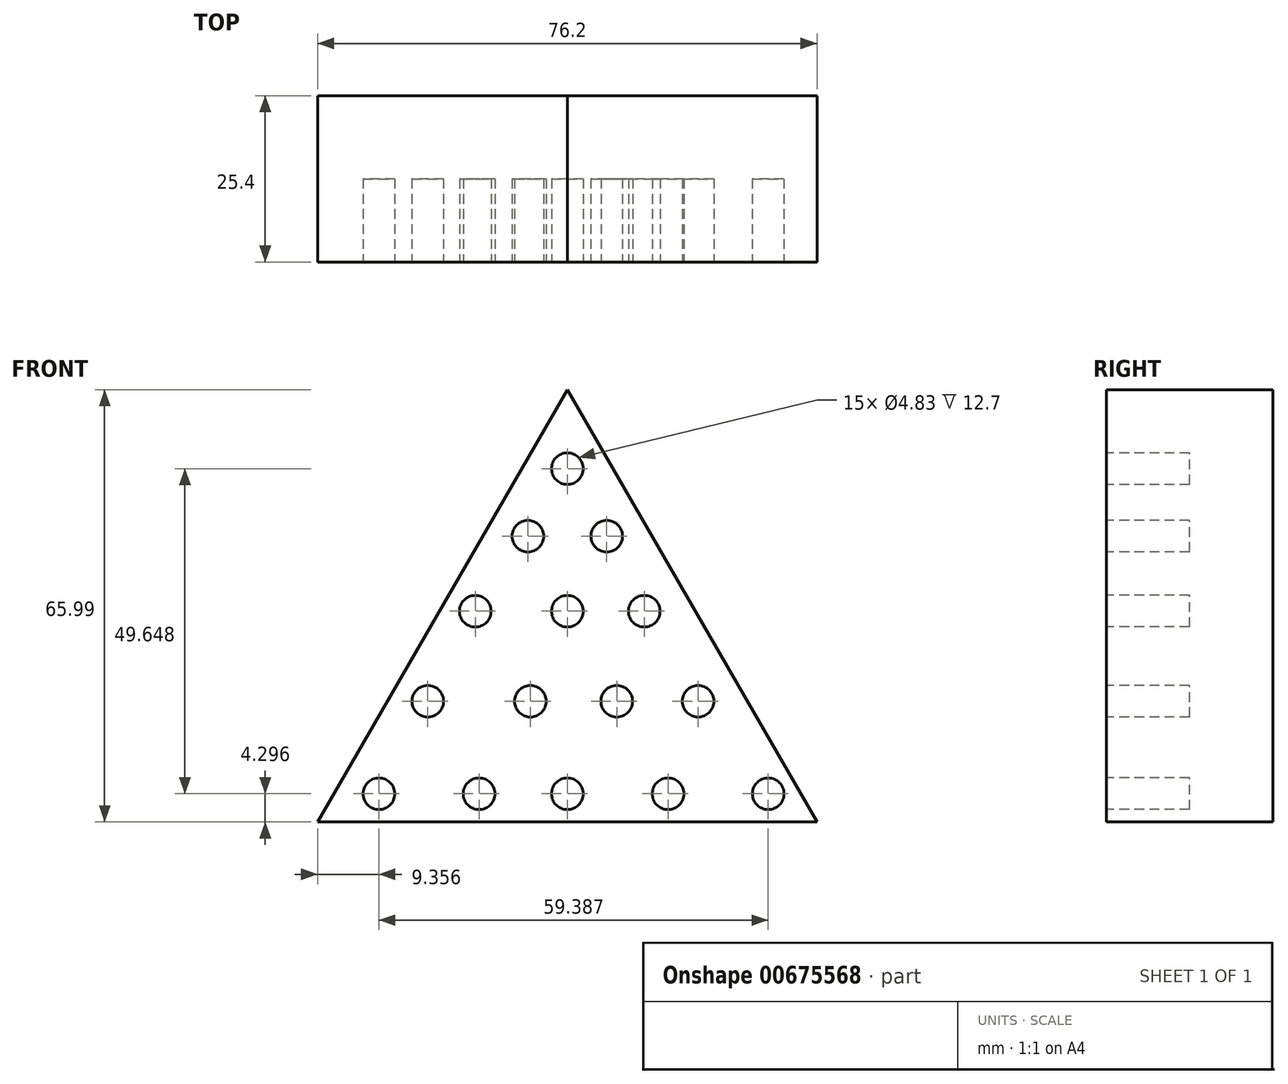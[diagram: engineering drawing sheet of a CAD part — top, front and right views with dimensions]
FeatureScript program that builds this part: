
annotation { "Feature Type Name" : "Feature", "Feature Type Description" : "" }
export const myFeature = defineFeature(function(context is Context, id is Id, definition is map)
    precondition{}
    {
        {
            var Q0;
            Q0=qCreatedBy(makeId("Front.planeOp"),FACE);
            var sketch = newSketch(context, id + "F0", { "sketchPlane" : qUnion([Q0])});
            skLineSegment(sketch, "E0", {"start": v(-73.23, 0) * mm, "end": v(2.97, 0) * mm});
            skLineSegment(sketch, "E1", {"start": v(2.97, 0) * mm, "end": v(-35.13, 66) * mm});
            skLineSegment(sketch, "E2", {"start": v(-35.13, 66) * mm, "end": v(-73.23, 0) * mm});
            skSolve(sketch);
        }
        {
            var Q0;
            Q0 = qSketchRegion(id + "F0", true);
            extrude(context, id + "F1", {"entities" : qUnion([Q0]), "depth" : 25.4 * mm, "offsetDistance" : 25.4 * mm});
        }
        {
            var Q0;
            Q0=makeQuery(id+"F1.opExtrude","CAP_FACE",FACE,{"disambiguationData":[OSD([sQuery(id+"F0.wireOp",EDGE,"E0"),sQuery(id+"F0.wireOp",EDGE,"E1"),sQuery(id+"F0.wireOp",EDGE,"E2")])],"isStart":false});
            var sketch = newSketch(context, id + "F2", { "sketchPlane" : qUnion([Q0])});
            skCircle(sketch, "E3", {"center": v(-63.87, 4.3) * mm, "radius": 2.41 * mm});
            skCircle(sketch, "E4", {"center": v(-48.6, 4.3) * mm, "radius": 2.41 * mm});
            skCircle(sketch, "E5", {"center": v(-35.13, 4.3) * mm, "radius": 2.41 * mm});
            skCircle(sketch, "E6", {"center": v(-19.76, 4.3) * mm, "radius": 2.41 * mm});
            skCircle(sketch, "E7", {"center": v(-4.49, 4.3) * mm, "radius": 2.41 * mm});
            skSolve(sketch);
        }
        {
            var Q0;
            Q0 = qSketchRegion(id + "F2", true);
            extrude(context, id + "F3", {"entities" : qUnion([Q0]), "operationType" : NewBodyOperationType.REMOVE, "oppositeDirection" : true, "depth" : 12.7 * mm, "offsetDistance" : 25.4 * mm});
        }
        {
            var Q0;
            Q0=makeQuery(id+"F1.opExtrude","CAP_FACE",FACE,{"disambiguationData":[OSD([sQuery(id+"F0.wireOp",EDGE,"E0"),sQuery(id+"F0.wireOp",EDGE,"E1"),sQuery(id+"F0.wireOp",EDGE,"E2")])],"isStart":false});
            var sketch = newSketch(context, id + "F4", { "sketchPlane" : qUnion([Q0])});
            skCircle(sketch, "E8", {"center": v(-56.43, 18.43) * mm, "radius": 2.41 * mm});
            skCircle(sketch, "E9", {"center": v(-40.77, 18.43) * mm, "radius": 2.41 * mm});
            skCircle(sketch, "E10", {"center": v(-27.6, 18.43) * mm, "radius": 2.41 * mm});
            skCircle(sketch, "E11", {"center": v(-15.18, 18.43) * mm, "radius": 2.41 * mm});
            skCircle(sketch, "E12", {"center": v(-23.4, 32.18) * mm, "radius": 2.41 * mm});
            skCircle(sketch, "E13", {"center": v(-35.13, 32.18) * mm, "radius": 2.41 * mm});
            skCircle(sketch, "E14", {"center": v(-49.17, 32.18) * mm, "radius": 2.41 * mm});
            skCircle(sketch, "E15", {"center": v(-41.15, 43.63) * mm, "radius": 2.41 * mm});
            skCircle(sketch, "E16", {"center": v(-29.12, 43.63) * mm, "radius": 2.41 * mm});
            skCircle(sketch, "E17", {"center": v(-35.13, 53.94) * mm, "radius": 2.41 * mm});
            skSolve(sketch);
        }
        {
            var Q0;
            Q0 = qSketchRegion(id + "F4", true);
            extrude(context, id + "F5", {"entities" : qUnion([Q0]), "operationType" : NewBodyOperationType.REMOVE, "oppositeDirection" : true, "depth" : 12.7 * mm, "offsetDistance" : 25.4 * mm});
        }
    });
